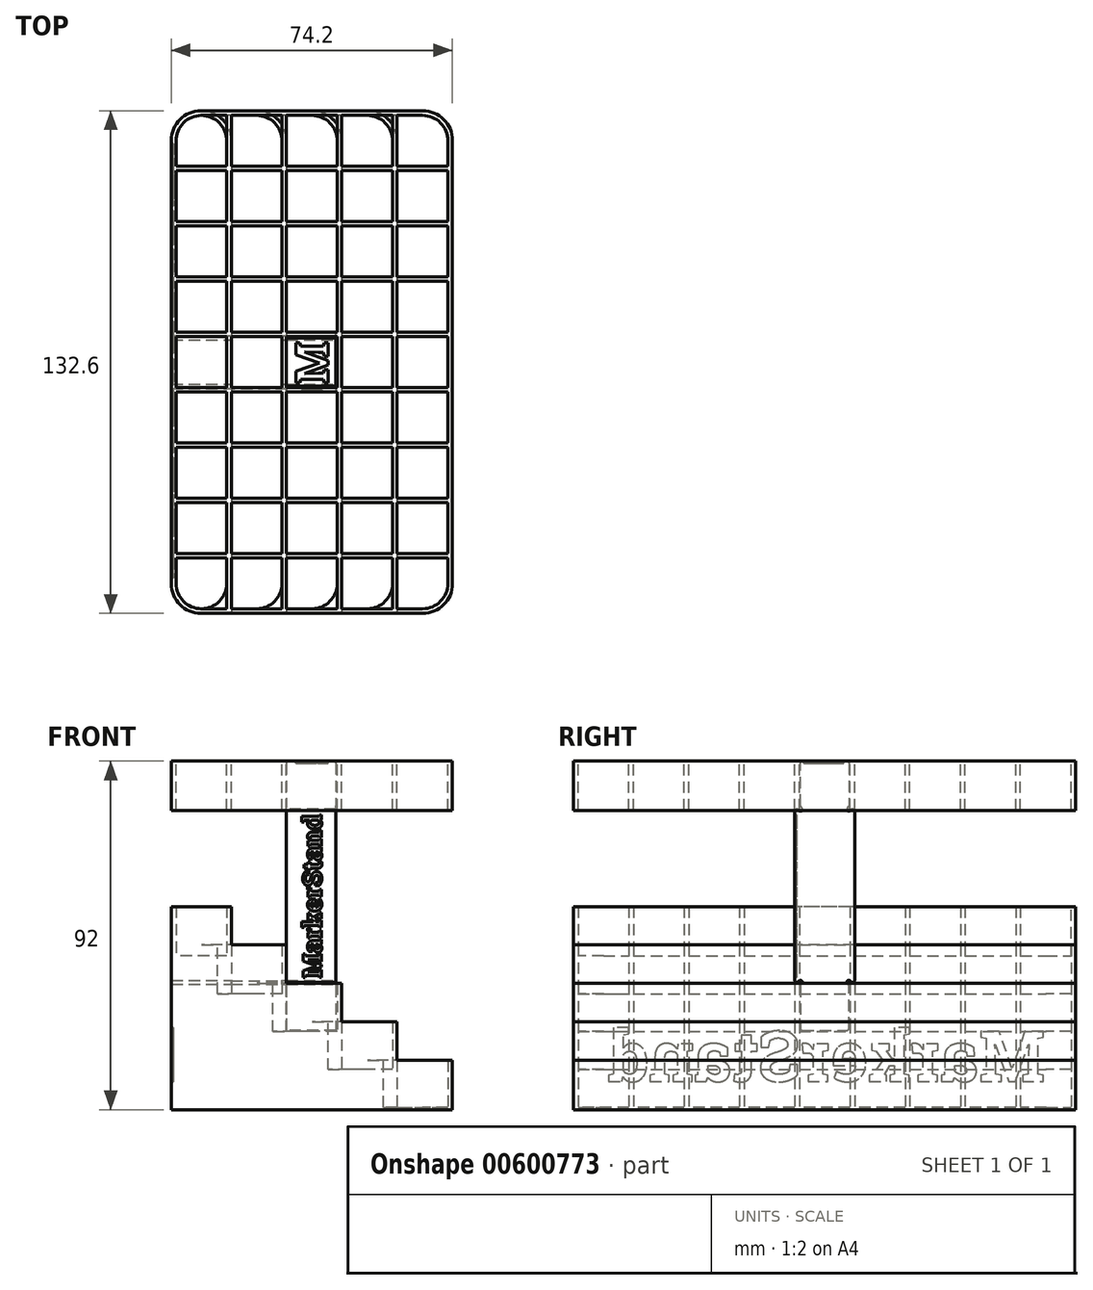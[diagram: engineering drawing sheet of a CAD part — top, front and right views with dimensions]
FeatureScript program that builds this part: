
annotation { "Feature Type Name" : "Feature", "Feature Type Description" : "" }
export const myFeature = defineFeature(function(context is Context, id is Id, definition is map)
    precondition{}
    {
        {
            var Q0;
            Q0=qCreatedBy(makeId("Top.planeOp"),FACE);
            var sketch = newSketch(context, id + "F0", { "sketchPlane" : qUnion([Q0])});
            skLineSegment(sketch, "E0.bottom", {"start": v(-37.1, 66.3) * mm, "end": v(37.1, 66.3) * mm});
            skLineSegment(sketch, "E0.top", {"start": v(-37.1, -66.3) * mm, "end": v(37.1, -66.3) * mm});
            skLineSegment(sketch, "E0.left", {"start": v(-37.1, 66.3) * mm, "end": v(-37.1, -66.3) * mm});
            skLineSegment(sketch, "E0.right", {"start": v(37.1, 66.3) * mm, "end": v(37.1, -66.3) * mm});
            skPoint(sketch, "E0.middle", {"position": v(0, 0) * mm});
            skLineSegment(sketch, "E1.bottom", {"start": v(-35.9, 65.1) * mm, "end": v(-22.5, 65.1) * mm});
            skLineSegment(sketch, "E1.top", {"start": v(-35.9, 51.7) * mm, "end": v(-22.5, 51.7) * mm});
            skLineSegment(sketch, "E1.left", {"start": v(-35.9, 65.1) * mm, "end": v(-35.9, 51.7) * mm});
            skLineSegment(sketch, "E1.right", {"start": v(-22.5, 65.1) * mm, "end": v(-22.5, 51.7) * mm});
            skLineSegment(sketch, "E2.0.1.0", {"start": v(-35.9, 37.1) * mm, "end": v(-22.5, 37.1) * mm});
            skLineSegment(sketch, "E2.0.1.1", {"start": v(-22.5, 50.5) * mm, "end": v(-22.5, 37.1) * mm});
            skLineSegment(sketch, "E2.0.1.2", {"start": v(-35.9, 50.5) * mm, "end": v(-22.5, 50.5) * mm});
            skLineSegment(sketch, "E2.0.1.3", {"start": v(-35.9, 50.5) * mm, "end": v(-35.9, 37.1) * mm});
            skLineSegment(sketch, "E2.0.2.0", {"start": v(-35.9, 22.5) * mm, "end": v(-22.5, 22.5) * mm});
            skLineSegment(sketch, "E2.0.2.1", {"start": v(-22.5, 35.9) * mm, "end": v(-22.5, 22.5) * mm});
            skLineSegment(sketch, "E2.0.2.2", {"start": v(-35.9, 35.9) * mm, "end": v(-22.5, 35.9) * mm});
            skLineSegment(sketch, "E2.0.2.3", {"start": v(-35.9, 35.9) * mm, "end": v(-35.9, 22.5) * mm});
            skLineSegment(sketch, "E2.0.3.0", {"start": v(-35.9, 7.9) * mm, "end": v(-22.5, 7.9) * mm});
            skLineSegment(sketch, "E2.0.3.1", {"start": v(-22.5, 21.3) * mm, "end": v(-22.5, 7.9) * mm});
            skLineSegment(sketch, "E2.0.3.2", {"start": v(-35.9, 21.3) * mm, "end": v(-22.5, 21.3) * mm});
            skLineSegment(sketch, "E2.0.3.3", {"start": v(-35.9, 21.3) * mm, "end": v(-35.9, 7.9) * mm});
            skLineSegment(sketch, "E2.0.4.0", {"start": v(-35.9, -6.7) * mm, "end": v(-22.5, -6.7) * mm});
            skLineSegment(sketch, "E2.0.4.1", {"start": v(-22.5, 6.7) * mm, "end": v(-22.5, -6.7) * mm});
            skLineSegment(sketch, "E2.0.4.2", {"start": v(-35.9, 6.7) * mm, "end": v(-22.5, 6.7) * mm});
            skLineSegment(sketch, "E2.0.4.3", {"start": v(-35.9, 6.7) * mm, "end": v(-35.9, -6.7) * mm});
            skLineSegment(sketch, "E2.0.5.0", {"start": v(-35.9, -21.3) * mm, "end": v(-22.5, -21.3) * mm});
            skLineSegment(sketch, "E2.0.5.1", {"start": v(-22.5, -7.9) * mm, "end": v(-22.5, -21.3) * mm});
            skLineSegment(sketch, "E2.0.5.2", {"start": v(-35.9, -7.9) * mm, "end": v(-22.5, -7.9) * mm});
            skLineSegment(sketch, "E2.0.5.3", {"start": v(-35.9, -7.9) * mm, "end": v(-35.9, -21.3) * mm});
            skLineSegment(sketch, "E2.0.6.0", {"start": v(-35.9, -35.9) * mm, "end": v(-22.5, -35.9) * mm});
            skLineSegment(sketch, "E2.0.6.1", {"start": v(-22.5, -22.5) * mm, "end": v(-22.5, -35.9) * mm});
            skLineSegment(sketch, "E2.0.6.2", {"start": v(-35.9, -22.5) * mm, "end": v(-22.5, -22.5) * mm});
            skLineSegment(sketch, "E2.0.6.3", {"start": v(-35.9, -22.5) * mm, "end": v(-35.9, -35.9) * mm});
            skLineSegment(sketch, "E2.0.7.0", {"start": v(-35.9, -50.5) * mm, "end": v(-22.5, -50.5) * mm});
            skLineSegment(sketch, "E2.0.7.1", {"start": v(-22.5, -37.1) * mm, "end": v(-22.5, -50.5) * mm});
            skLineSegment(sketch, "E2.0.7.2", {"start": v(-35.9, -37.1) * mm, "end": v(-22.5, -37.1) * mm});
            skLineSegment(sketch, "E2.0.7.3", {"start": v(-35.9, -37.1) * mm, "end": v(-35.9, -50.5) * mm});
            skLineSegment(sketch, "E2.0.8.0", {"start": v(-35.9, -65.1) * mm, "end": v(-22.5, -65.1) * mm});
            skLineSegment(sketch, "E2.0.8.1", {"start": v(-22.5, -51.7) * mm, "end": v(-22.5, -65.1) * mm});
            skLineSegment(sketch, "E2.0.8.2", {"start": v(-35.9, -51.7) * mm, "end": v(-22.5, -51.7) * mm});
            skLineSegment(sketch, "E2.0.8.3", {"start": v(-35.9, -51.7) * mm, "end": v(-35.9, -65.1) * mm});
            skLineSegment(sketch, "E2.1.0.0", {"start": v(-21.3, 51.7) * mm, "end": v(-7.9, 51.7) * mm});
            skLineSegment(sketch, "E2.1.0.1", {"start": v(-7.9, 65.1) * mm, "end": v(-7.9, 51.7) * mm});
            skLineSegment(sketch, "E2.1.0.2", {"start": v(-21.3, 65.1) * mm, "end": v(-7.9, 65.1) * mm});
            skLineSegment(sketch, "E2.1.0.3", {"start": v(-21.3, 65.1) * mm, "end": v(-21.3, 51.7) * mm});
            skLineSegment(sketch, "E2.1.1.0", {"start": v(-21.3, 37.1) * mm, "end": v(-7.9, 37.1) * mm});
            skLineSegment(sketch, "E2.1.1.1", {"start": v(-7.9, 50.5) * mm, "end": v(-7.9, 37.1) * mm});
            skLineSegment(sketch, "E2.1.1.2", {"start": v(-21.3, 50.5) * mm, "end": v(-7.9, 50.5) * mm});
            skLineSegment(sketch, "E2.1.1.3", {"start": v(-21.3, 50.5) * mm, "end": v(-21.3, 37.1) * mm});
            skLineSegment(sketch, "E2.1.2.0", {"start": v(-21.3, 22.5) * mm, "end": v(-7.9, 22.5) * mm});
            skLineSegment(sketch, "E2.1.2.1", {"start": v(-7.9, 35.9) * mm, "end": v(-7.9, 22.5) * mm});
            skLineSegment(sketch, "E2.1.2.2", {"start": v(-21.3, 35.9) * mm, "end": v(-7.9, 35.9) * mm});
            skLineSegment(sketch, "E2.1.2.3", {"start": v(-21.3, 35.9) * mm, "end": v(-21.3, 22.5) * mm});
            skLineSegment(sketch, "E2.1.3.0", {"start": v(-21.3, 7.9) * mm, "end": v(-7.9, 7.9) * mm});
            skLineSegment(sketch, "E2.1.3.1", {"start": v(-7.9, 21.3) * mm, "end": v(-7.9, 7.9) * mm});
            skLineSegment(sketch, "E2.1.3.2", {"start": v(-21.3, 21.3) * mm, "end": v(-7.9, 21.3) * mm});
            skLineSegment(sketch, "E2.1.3.3", {"start": v(-21.3, 21.3) * mm, "end": v(-21.3, 7.9) * mm});
            skLineSegment(sketch, "E2.1.4.0", {"start": v(-21.3, -6.7) * mm, "end": v(-7.9, -6.7) * mm});
            skLineSegment(sketch, "E2.1.4.1", {"start": v(-7.9, 6.7) * mm, "end": v(-7.9, -6.7) * mm});
            skLineSegment(sketch, "E2.1.4.2", {"start": v(-21.3, 6.7) * mm, "end": v(-7.9, 6.7) * mm});
            skLineSegment(sketch, "E2.1.4.3", {"start": v(-21.3, 6.7) * mm, "end": v(-21.3, -6.7) * mm});
            skLineSegment(sketch, "E2.1.5.0", {"start": v(-21.3, -21.3) * mm, "end": v(-7.9, -21.3) * mm});
            skLineSegment(sketch, "E2.1.5.1", {"start": v(-7.9, -7.9) * mm, "end": v(-7.9, -21.3) * mm});
            skLineSegment(sketch, "E2.1.5.2", {"start": v(-21.3, -7.9) * mm, "end": v(-7.9, -7.9) * mm});
            skLineSegment(sketch, "E2.1.5.3", {"start": v(-21.3, -7.9) * mm, "end": v(-21.3, -21.3) * mm});
            skLineSegment(sketch, "E2.1.6.0", {"start": v(-21.3, -35.9) * mm, "end": v(-7.9, -35.9) * mm});
            skLineSegment(sketch, "E2.1.6.1", {"start": v(-7.9, -22.5) * mm, "end": v(-7.9, -35.9) * mm});
            skLineSegment(sketch, "E2.1.6.2", {"start": v(-21.3, -22.5) * mm, "end": v(-7.9, -22.5) * mm});
            skLineSegment(sketch, "E2.1.6.3", {"start": v(-21.3, -22.5) * mm, "end": v(-21.3, -35.9) * mm});
            skLineSegment(sketch, "E2.1.7.0", {"start": v(-21.3, -50.5) * mm, "end": v(-7.9, -50.5) * mm});
            skLineSegment(sketch, "E2.1.7.1", {"start": v(-7.9, -37.1) * mm, "end": v(-7.9, -50.5) * mm});
            skLineSegment(sketch, "E2.1.7.2", {"start": v(-21.3, -37.1) * mm, "end": v(-7.9, -37.1) * mm});
            skLineSegment(sketch, "E2.1.7.3", {"start": v(-21.3, -37.1) * mm, "end": v(-21.3, -50.5) * mm});
            skLineSegment(sketch, "E2.1.8.0", {"start": v(-21.3, -65.1) * mm, "end": v(-7.9, -65.1) * mm});
            skLineSegment(sketch, "E2.1.8.1", {"start": v(-7.9, -51.7) * mm, "end": v(-7.9, -65.1) * mm});
            skLineSegment(sketch, "E2.1.8.2", {"start": v(-21.3, -51.7) * mm, "end": v(-7.9, -51.7) * mm});
            skLineSegment(sketch, "E2.1.8.3", {"start": v(-21.3, -51.7) * mm, "end": v(-21.3, -65.1) * mm});
            skLineSegment(sketch, "E2.2.0.0", {"start": v(-6.7, 51.7) * mm, "end": v(6.7, 51.7) * mm});
            skLineSegment(sketch, "E2.2.0.1", {"start": v(6.7, 65.1) * mm, "end": v(6.7, 51.7) * mm});
            skLineSegment(sketch, "E2.2.0.2", {"start": v(-6.7, 65.1) * mm, "end": v(6.7, 65.1) * mm});
            skLineSegment(sketch, "E2.2.0.3", {"start": v(-6.7, 65.1) * mm, "end": v(-6.7, 51.7) * mm});
            skLineSegment(sketch, "E2.2.1.0", {"start": v(-6.7, 37.1) * mm, "end": v(6.7, 37.1) * mm});
            skLineSegment(sketch, "E2.2.1.1", {"start": v(6.7, 50.5) * mm, "end": v(6.7, 37.1) * mm});
            skLineSegment(sketch, "E2.2.1.2", {"start": v(-6.7, 50.5) * mm, "end": v(6.7, 50.5) * mm});
            skLineSegment(sketch, "E2.2.1.3", {"start": v(-6.7, 50.5) * mm, "end": v(-6.7, 37.1) * mm});
            skLineSegment(sketch, "E2.2.2.0", {"start": v(-6.7, 22.5) * mm, "end": v(6.7, 22.5) * mm});
            skLineSegment(sketch, "E2.2.2.1", {"start": v(6.7, 35.9) * mm, "end": v(6.7, 22.5) * mm});
            skLineSegment(sketch, "E2.2.2.2", {"start": v(-6.7, 35.9) * mm, "end": v(6.7, 35.9) * mm});
            skLineSegment(sketch, "E2.2.2.3", {"start": v(-6.7, 35.9) * mm, "end": v(-6.7, 22.5) * mm});
            skLineSegment(sketch, "E2.2.3.0", {"start": v(-6.7, 7.9) * mm, "end": v(6.7, 7.9) * mm});
            skLineSegment(sketch, "E2.2.3.1", {"start": v(6.7, 21.3) * mm, "end": v(6.7, 7.9) * mm});
            skLineSegment(sketch, "E2.2.3.2", {"start": v(-6.7, 21.3) * mm, "end": v(6.7, 21.3) * mm});
            skLineSegment(sketch, "E2.2.3.3", {"start": v(-6.7, 21.3) * mm, "end": v(-6.7, 7.9) * mm});
            skLineSegment(sketch, "E2.2.4.0", {"start": v(-6.7, -6.7) * mm, "end": v(6.7, -6.7) * mm});
            skLineSegment(sketch, "E2.2.4.1", {"start": v(6.7, 6.7) * mm, "end": v(6.7, -6.7) * mm});
            skLineSegment(sketch, "E2.2.4.2", {"start": v(-6.7, 6.7) * mm, "end": v(6.7, 6.7) * mm});
            skLineSegment(sketch, "E2.2.4.3", {"start": v(-6.7, 6.7) * mm, "end": v(-6.7, -6.7) * mm});
            skLineSegment(sketch, "E2.2.5.0", {"start": v(-6.7, -21.3) * mm, "end": v(6.7, -21.3) * mm});
            skLineSegment(sketch, "E2.2.5.1", {"start": v(6.7, -7.9) * mm, "end": v(6.7, -21.3) * mm});
            skLineSegment(sketch, "E2.2.5.2", {"start": v(-6.7, -7.9) * mm, "end": v(6.7, -7.9) * mm});
            skLineSegment(sketch, "E2.2.5.3", {"start": v(-6.7, -7.9) * mm, "end": v(-6.7, -21.3) * mm});
            skLineSegment(sketch, "E2.2.6.0", {"start": v(-6.7, -35.9) * mm, "end": v(6.7, -35.9) * mm});
            skLineSegment(sketch, "E2.2.6.1", {"start": v(6.7, -22.5) * mm, "end": v(6.7, -35.9) * mm});
            skLineSegment(sketch, "E2.2.6.2", {"start": v(-6.7, -22.5) * mm, "end": v(6.7, -22.5) * mm});
            skLineSegment(sketch, "E2.2.6.3", {"start": v(-6.7, -22.5) * mm, "end": v(-6.7, -35.9) * mm});
            skLineSegment(sketch, "E2.2.7.0", {"start": v(-6.7, -50.5) * mm, "end": v(6.7, -50.5) * mm});
            skLineSegment(sketch, "E2.2.7.1", {"start": v(6.7, -37.1) * mm, "end": v(6.7, -50.5) * mm});
            skLineSegment(sketch, "E2.2.7.2", {"start": v(-6.7, -37.1) * mm, "end": v(6.7, -37.1) * mm});
            skLineSegment(sketch, "E2.2.7.3", {"start": v(-6.7, -37.1) * mm, "end": v(-6.7, -50.5) * mm});
            skLineSegment(sketch, "E2.2.8.0", {"start": v(-6.7, -65.1) * mm, "end": v(6.7, -65.1) * mm});
            skLineSegment(sketch, "E2.2.8.1", {"start": v(6.7, -51.7) * mm, "end": v(6.7, -65.1) * mm});
            skLineSegment(sketch, "E2.2.8.2", {"start": v(-6.7, -51.7) * mm, "end": v(6.7, -51.7) * mm});
            skLineSegment(sketch, "E2.2.8.3", {"start": v(-6.7, -51.7) * mm, "end": v(-6.7, -65.1) * mm});
            skLineSegment(sketch, "E2.3.0.0", {"start": v(7.9, 51.7) * mm, "end": v(21.3, 51.7) * mm});
            skLineSegment(sketch, "E2.3.0.1", {"start": v(21.3, 65.1) * mm, "end": v(21.3, 51.7) * mm});
            skLineSegment(sketch, "E2.3.0.2", {"start": v(7.9, 65.1) * mm, "end": v(21.3, 65.1) * mm});
            skLineSegment(sketch, "E2.3.0.3", {"start": v(7.9, 65.1) * mm, "end": v(7.9, 51.7) * mm});
            skLineSegment(sketch, "E2.3.1.0", {"start": v(7.9, 37.1) * mm, "end": v(21.3, 37.1) * mm});
            skLineSegment(sketch, "E2.3.1.1", {"start": v(21.3, 50.5) * mm, "end": v(21.3, 37.1) * mm});
            skLineSegment(sketch, "E2.3.1.2", {"start": v(7.9, 50.5) * mm, "end": v(21.3, 50.5) * mm});
            skLineSegment(sketch, "E2.3.1.3", {"start": v(7.9, 50.5) * mm, "end": v(7.9, 37.1) * mm});
            skLineSegment(sketch, "E2.3.2.0", {"start": v(7.9, 22.5) * mm, "end": v(21.3, 22.5) * mm});
            skLineSegment(sketch, "E2.3.2.1", {"start": v(21.3, 35.9) * mm, "end": v(21.3, 22.5) * mm});
            skLineSegment(sketch, "E2.3.2.2", {"start": v(7.9, 35.9) * mm, "end": v(21.3, 35.9) * mm});
            skLineSegment(sketch, "E2.3.2.3", {"start": v(7.9, 35.9) * mm, "end": v(7.9, 22.5) * mm});
            skLineSegment(sketch, "E2.3.3.0", {"start": v(7.9, 7.9) * mm, "end": v(21.3, 7.9) * mm});
            skLineSegment(sketch, "E2.3.3.1", {"start": v(21.3, 21.3) * mm, "end": v(21.3, 7.9) * mm});
            skLineSegment(sketch, "E2.3.3.2", {"start": v(7.9, 21.3) * mm, "end": v(21.3, 21.3) * mm});
            skLineSegment(sketch, "E2.3.3.3", {"start": v(7.9, 21.3) * mm, "end": v(7.9, 7.9) * mm});
            skLineSegment(sketch, "E2.3.4.0", {"start": v(7.9, -6.7) * mm, "end": v(21.3, -6.7) * mm});
            skLineSegment(sketch, "E2.3.4.1", {"start": v(21.3, 6.7) * mm, "end": v(21.3, -6.7) * mm});
            skLineSegment(sketch, "E2.3.4.2", {"start": v(7.9, 6.7) * mm, "end": v(21.3, 6.7) * mm});
            skLineSegment(sketch, "E2.3.4.3", {"start": v(7.9, 6.7) * mm, "end": v(7.9, -6.7) * mm});
            skLineSegment(sketch, "E2.3.5.0", {"start": v(7.9, -21.3) * mm, "end": v(21.3, -21.3) * mm});
            skLineSegment(sketch, "E2.3.5.1", {"start": v(21.3, -7.9) * mm, "end": v(21.3, -21.3) * mm});
            skLineSegment(sketch, "E2.3.5.2", {"start": v(7.9, -7.9) * mm, "end": v(21.3, -7.9) * mm});
            skLineSegment(sketch, "E2.3.5.3", {"start": v(7.9, -7.9) * mm, "end": v(7.9, -21.3) * mm});
            skLineSegment(sketch, "E2.3.6.0", {"start": v(7.9, -35.9) * mm, "end": v(21.3, -35.9) * mm});
            skLineSegment(sketch, "E2.3.6.1", {"start": v(21.3, -22.5) * mm, "end": v(21.3, -35.9) * mm});
            skLineSegment(sketch, "E2.3.6.2", {"start": v(7.9, -22.5) * mm, "end": v(21.3, -22.5) * mm});
            skLineSegment(sketch, "E2.3.6.3", {"start": v(7.9, -22.5) * mm, "end": v(7.9, -35.9) * mm});
            skLineSegment(sketch, "E2.3.7.0", {"start": v(7.9, -50.5) * mm, "end": v(21.3, -50.5) * mm});
            skLineSegment(sketch, "E2.3.7.1", {"start": v(21.3, -37.1) * mm, "end": v(21.3, -50.5) * mm});
            skLineSegment(sketch, "E2.3.7.2", {"start": v(7.9, -37.1) * mm, "end": v(21.3, -37.1) * mm});
            skLineSegment(sketch, "E2.3.7.3", {"start": v(7.9, -37.1) * mm, "end": v(7.9, -50.5) * mm});
            skLineSegment(sketch, "E2.3.8.0", {"start": v(7.9, -65.1) * mm, "end": v(21.3, -65.1) * mm});
            skLineSegment(sketch, "E2.3.8.1", {"start": v(21.3, -51.7) * mm, "end": v(21.3, -65.1) * mm});
            skLineSegment(sketch, "E2.3.8.2", {"start": v(7.9, -51.7) * mm, "end": v(21.3, -51.7) * mm});
            skLineSegment(sketch, "E2.3.8.3", {"start": v(7.9, -51.7) * mm, "end": v(7.9, -65.1) * mm});
            skLineSegment(sketch, "E2.4.0.0", {"start": v(22.5, 51.7) * mm, "end": v(35.9, 51.7) * mm});
            skLineSegment(sketch, "E2.4.0.1", {"start": v(35.9, 65.1) * mm, "end": v(35.9, 51.7) * mm});
            skLineSegment(sketch, "E2.4.0.2", {"start": v(22.5, 65.1) * mm, "end": v(35.9, 65.1) * mm});
            skLineSegment(sketch, "E2.4.0.3", {"start": v(22.5, 65.1) * mm, "end": v(22.5, 51.7) * mm});
            skLineSegment(sketch, "E2.4.1.0", {"start": v(22.5, 37.1) * mm, "end": v(35.9, 37.1) * mm});
            skLineSegment(sketch, "E2.4.1.1", {"start": v(35.9, 50.5) * mm, "end": v(35.9, 37.1) * mm});
            skLineSegment(sketch, "E2.4.1.2", {"start": v(22.5, 50.5) * mm, "end": v(35.9, 50.5) * mm});
            skLineSegment(sketch, "E2.4.1.3", {"start": v(22.5, 50.5) * mm, "end": v(22.5, 37.1) * mm});
            skLineSegment(sketch, "E2.4.2.0", {"start": v(22.5, 22.5) * mm, "end": v(35.9, 22.5) * mm});
            skLineSegment(sketch, "E2.4.2.1", {"start": v(35.9, 35.9) * mm, "end": v(35.9, 22.5) * mm});
            skLineSegment(sketch, "E2.4.2.2", {"start": v(22.5, 35.9) * mm, "end": v(35.9, 35.9) * mm});
            skLineSegment(sketch, "E2.4.2.3", {"start": v(22.5, 35.9) * mm, "end": v(22.5, 22.5) * mm});
            skLineSegment(sketch, "E2.4.3.0", {"start": v(22.5, 7.9) * mm, "end": v(35.9, 7.9) * mm});
            skLineSegment(sketch, "E2.4.3.1", {"start": v(35.9, 21.3) * mm, "end": v(35.9, 7.9) * mm});
            skLineSegment(sketch, "E2.4.3.2", {"start": v(22.5, 21.3) * mm, "end": v(35.9, 21.3) * mm});
            skLineSegment(sketch, "E2.4.3.3", {"start": v(22.5, 21.3) * mm, "end": v(22.5, 7.9) * mm});
            skLineSegment(sketch, "E2.4.4.0", {"start": v(22.5, -6.7) * mm, "end": v(35.9, -6.7) * mm});
            skLineSegment(sketch, "E2.4.4.1", {"start": v(35.9, 6.7) * mm, "end": v(35.9, -6.7) * mm});
            skLineSegment(sketch, "E2.4.4.2", {"start": v(22.5, 6.7) * mm, "end": v(35.9, 6.7) * mm});
            skLineSegment(sketch, "E2.4.4.3", {"start": v(22.5, 6.7) * mm, "end": v(22.5, -6.7) * mm});
            skLineSegment(sketch, "E2.4.5.0", {"start": v(22.5, -21.3) * mm, "end": v(35.9, -21.3) * mm});
            skLineSegment(sketch, "E2.4.5.1", {"start": v(35.9, -7.9) * mm, "end": v(35.9, -21.3) * mm});
            skLineSegment(sketch, "E2.4.5.2", {"start": v(22.5, -7.9) * mm, "end": v(35.9, -7.9) * mm});
            skLineSegment(sketch, "E2.4.5.3", {"start": v(22.5, -7.9) * mm, "end": v(22.5, -21.3) * mm});
            skLineSegment(sketch, "E2.4.6.0", {"start": v(22.5, -35.9) * mm, "end": v(35.9, -35.9) * mm});
            skLineSegment(sketch, "E2.4.6.1", {"start": v(35.9, -22.5) * mm, "end": v(35.9, -35.9) * mm});
            skLineSegment(sketch, "E2.4.6.2", {"start": v(22.5, -22.5) * mm, "end": v(35.9, -22.5) * mm});
            skLineSegment(sketch, "E2.4.6.3", {"start": v(22.5, -22.5) * mm, "end": v(22.5, -35.9) * mm});
            skLineSegment(sketch, "E2.4.7.0", {"start": v(22.5, -50.5) * mm, "end": v(35.9, -50.5) * mm});
            skLineSegment(sketch, "E2.4.7.1", {"start": v(35.9, -37.1) * mm, "end": v(35.9, -50.5) * mm});
            skLineSegment(sketch, "E2.4.7.2", {"start": v(22.5, -37.1) * mm, "end": v(35.9, -37.1) * mm});
            skLineSegment(sketch, "E2.4.7.3", {"start": v(22.5, -37.1) * mm, "end": v(22.5, -50.5) * mm});
            skLineSegment(sketch, "E2.4.8.0", {"start": v(22.5, -65.1) * mm, "end": v(35.9, -65.1) * mm});
            skLineSegment(sketch, "E2.4.8.1", {"start": v(35.9, -51.7) * mm, "end": v(35.9, -65.1) * mm});
            skLineSegment(sketch, "E2.4.8.2", {"start": v(22.5, -51.7) * mm, "end": v(35.9, -51.7) * mm});
            skLineSegment(sketch, "E2.4.8.3", {"start": v(22.5, -51.7) * mm, "end": v(22.5, -65.1) * mm});
            skLineSegment(sketch, "E2.direction1", {"start": v(-35.9, 51.7) * mm, "end": v(-21.3, 51.7) * mm, "construction": true});
            skLineSegment(sketch, "E2.direction2", {"start": v(-35.9, 51.7) * mm, "end": v(-35.9, 37.1) * mm, "construction": true});
            skSolve(sketch);
        }
        {
            var Q0;
            Q0 = qSketchRegion(id + "F0", true);
            extrude(context, id + "F1", {"entities" : qUnion([Q0]), "depth" : 53 * mm, "offsetDistance" : 25 * mm});
        }
        {
            var Q0;
            Q0=makeQuery(id+"F1.opExtrude","SWEPT_FACE",FACE,{"disambiguationData":[OSD([sQuery(id+"F0.wireOp",EDGE,"E0.bottom")])]});
            var sketch = newSketch(context, id + "F2", { "sketchPlane" : qUnion([Q0])});
            skLineSegment(sketch, "E3", {"start": v(37.1, -0.6) * mm, "end": v(-37.1, -0.6) * mm});
            skLineSegment(sketch, "E4", {"start": v(-37.1, -0.6) * mm, "end": v(-37.1, 0) * mm});
            skLineSegment(sketch, "E5", {"start": v(-37.1, 0) * mm, "end": v(-22.5, 0) * mm});
            skLineSegment(sketch, "E6", {"start": v(-22.5, 0) * mm, "end": v(-22.5, 10) * mm});
            skLineSegment(sketch, "E7", {"start": v(-22.5, 10) * mm, "end": v(-7.9, 10) * mm});
            skLineSegment(sketch, "E8", {"start": v(-7.9, 10) * mm, "end": v(-7.9, 20) * mm});
            skLineSegment(sketch, "E9", {"start": v(-7.9, 20) * mm, "end": v(6.7, 20) * mm});
            skLineSegment(sketch, "E10", {"start": v(6.7, 20) * mm, "end": v(6.7, 30) * mm});
            skLineSegment(sketch, "E11", {"start": v(6.7, 30) * mm, "end": v(21.3, 30) * mm});
            skLineSegment(sketch, "E12", {"start": v(21.3, 30) * mm, "end": v(21.3, 40) * mm});
            skLineSegment(sketch, "E13", {"start": v(21.3, 40) * mm, "end": v(37.1, 40) * mm});
            skLineSegment(sketch, "E14", {"start": v(37.1, 40) * mm, "end": v(37.1, -0.6) * mm});
            skSolve(sketch);
        }
        {
            var Q0;
            Q0 = qSketchRegion(id + "F2", true);
            var Q1;
            Q1=makeQuery(id+"F1.opExtrude","SWEPT_FACE",FACE,{"disambiguationData":[OSD([sQuery(id+"F0.wireOp",EDGE,"E0.top")])]});
            extrude(context, id + "F3", {"entities" : qUnion([Q0]), "operationType" : NewBodyOperationType.ADD, "endBound" : BoundingType.UP_TO_SURFACE, "oppositeDirection" : true, "depth" : 25 * mm, "endBoundEntityFace" : qUnion([Q1]), "offsetDistance" : 25 * mm});
        }
        {
            var Q0;
            {var subQ0=sQuery(id+"F0.wireOp",EDGE,"E0.top");Q0=makeQuery(id+"F3.boolean.opBoolean","MERGE",FACE,{"derivedFrom":[makeQuery(id+"F1.opExtrude","SWEPT_FACE",FACE,{"disambiguationData":[OSD([subQ0])]}),makeQuery(id+"F3.opExtrude","CAP_FACE",FACE,{"disambiguationData":[OSD([subQ0])],"isStart":false})]});}
            var sketch = newSketch(context, id + "F4", { "sketchPlane" : qUnion([Q0])});
            skLineSegment(sketch, "E15", {"start": v(-21.3, 53) * mm, "end": v(-21.3, 42.85) * mm});
            skLineSegment(sketch, "E16", {"start": v(-21.3, 42.85) * mm, "end": v(-6.7, 42.85) * mm});
            skLineSegment(sketch, "E17", {"start": v(-6.7, 42.85) * mm, "end": v(-6.7, 32.7) * mm});
            skLineSegment(sketch, "E18", {"start": v(-6.7, 32.7) * mm, "end": v(7.9, 32.7) * mm});
            skLineSegment(sketch, "E19", {"start": v(7.9, 32.7) * mm, "end": v(7.9, 22.55) * mm});
            skLineSegment(sketch, "E20", {"start": v(7.9, 22.55) * mm, "end": v(22.5, 22.55) * mm});
            skLineSegment(sketch, "E21", {"start": v(22.5, 22.55) * mm, "end": v(22.5, 12.4) * mm});
            skLineSegment(sketch, "E22", {"start": v(22.5, 12.4) * mm, "end": v(37.1, 12.4) * mm});
            skLineSegment(sketch, "E23", {"start": v(37.1, 12.4) * mm, "end": v(37.1, 53) * mm});
            skLineSegment(sketch, "E24", {"start": v(37.1, 53) * mm, "end": v(-21.3, 53) * mm});
            skLineSegment(sketch, "E25", {"start": v(-21.3, 42.85) * mm, "end": v(7.9, 22.55) * mm, "construction": true});
            skSolve(sketch);
        }
        {
            var Q0;
            Q0 = qSketchRegion(id + "F4", true);
            extrude(context, id + "F5", {"entities" : qUnion([Q0]), "operationType" : NewBodyOperationType.REMOVE, "endBound" : BoundingType.THROUGH_ALL, "oppositeDirection" : true, "depth" : 25 * mm, "offsetDistance" : 25 * mm});
        }
        {
            var Q0;
            Q0=makeQuery(id+"F3.boolean.opBoolean","MERGE",FACE,{"derivedFrom":[makeQuery(id+"F1.opExtrude","SWEPT_FACE",FACE,{"disambiguationData":[OSD([sQuery(id+"F0.wireOp",EDGE,"E0.left")])]}),makeQuery(id+"F3.opExtrude","SWEPT_FACE",FACE,{"disambiguationData":[OSD([sQuery(id+"F2.wireOp",EDGE,"E14")])]})]});
            var sketch = newSketch(context, id + "F6", { "sketchPlane" : qUnion([Q0])});
            skLineSegment(sketch, "E26", {"start": v(0, 0) * mm, "end": v(0, 40) * mm, "construction": true});
            skText(sketch, "E27", { "text": "MarkerStand", "fontName": "RobotoSlab-Bold.ttf"});
            const initialGuessF6  = {"E27": [-0.0582, 0.0069, 1, 0, 0.01335]};
            skSetInitialGuess(sketch, initialGuessF6);
            skSolve(sketch);
        }
        {
            var Q0;
            Q0 = qSketchRegion(id + "F6", true);
            extrude(context, id + "F7", {"entities" : qUnion([Q0]), "operationType" : NewBodyOperationType.REMOVE, "oppositeDirection" : true, "depth" : 0.54 * mm, "offsetDistance" : 25 * mm});
        }
        {
            var Q0;
            Q0=makeQuery(id+"F1.opExtrude","SWEPT_EDGE",EDGE,{"disambiguationData":[OSD([sQuery(id+"F0.wireOp",EDGE,"E1.bottom"),sQuery(id+"F0.wireOp",EDGE,"E1.right")])]});
            var Q1;
            Q1=makeQuery(id+"F1.opExtrude","SWEPT_EDGE",EDGE,{"disambiguationData":[OSD([sQuery(id+"F0.wireOp",EDGE,"E2.1.0.1"),sQuery(id+"F0.wireOp",EDGE,"E2.1.0.2")])]});
            var Q2;
            Q2=makeQuery(id+"F1.opExtrude","SWEPT_EDGE",EDGE,{"disambiguationData":[OSD([sQuery(id+"F0.wireOp",EDGE,"E2.2.0.1"),sQuery(id+"F0.wireOp",EDGE,"E2.2.0.2")])]});
            var Q3;
            Q3=makeQuery(id+"F1.opExtrude","SWEPT_EDGE",EDGE,{"disambiguationData":[OSD([sQuery(id+"F0.wireOp",EDGE,"E2.3.0.1"),sQuery(id+"F0.wireOp",EDGE,"E2.3.0.2")])]});
            var Q4;
            Q4=makeQuery(id+"F1.opExtrude","SWEPT_EDGE",EDGE,{"disambiguationData":[OSD([sQuery(id+"F0.wireOp",EDGE,"E2.4.0.1"),sQuery(id+"F0.wireOp",EDGE,"E2.4.0.2")])]});
            var Q5;
            Q5=makeQuery(id+"F1.opExtrude","SWEPT_EDGE",EDGE,{"disambiguationData":[OSD([sQuery(id+"F0.wireOp",EDGE,"E2.4.8.0"),sQuery(id+"F0.wireOp",EDGE,"E2.4.8.1")])]});
            var Q6;
            Q6=makeQuery(id+"F1.opExtrude","SWEPT_EDGE",EDGE,{"disambiguationData":[OSD([sQuery(id+"F0.wireOp",EDGE,"E2.3.8.0"),sQuery(id+"F0.wireOp",EDGE,"E2.3.8.1")])]});
            var Q7;
            Q7=makeQuery(id+"F1.opExtrude","SWEPT_EDGE",EDGE,{"disambiguationData":[OSD([sQuery(id+"F0.wireOp",EDGE,"E2.2.8.0"),sQuery(id+"F0.wireOp",EDGE,"E2.2.8.1")])]});
            var Q8;
            Q8=makeQuery(id+"F1.opExtrude","SWEPT_EDGE",EDGE,{"disambiguationData":[OSD([sQuery(id+"F0.wireOp",EDGE,"E2.1.8.0"),sQuery(id+"F0.wireOp",EDGE,"E2.1.8.1")])]});
            var Q9;
            Q9=makeQuery(id+"F1.opExtrude","SWEPT_EDGE",EDGE,{"disambiguationData":[OSD([sQuery(id+"F0.wireOp",EDGE,"E2.0.8.0"),sQuery(id+"F0.wireOp",EDGE,"E2.0.8.1")])]});
            var Q10;
            Q10=makeQuery(id+"F1.opExtrude","SWEPT_EDGE",EDGE,{"disambiguationData":[OSD([sQuery(id+"F0.wireOp",EDGE,"E2.0.8.0"),sQuery(id+"F0.wireOp",EDGE,"E2.0.8.3")])]});
            var Q11;
            Q11=makeQuery(id+"F1.opExtrude","SWEPT_EDGE",EDGE,{"disambiguationData":[OSD([sQuery(id+"F0.wireOp",EDGE,"E1.bottom"),sQuery(id+"F0.wireOp",EDGE,"E1.left")])]});
            fillet(context, id + "F8", {"entities" : qUnion([Q0, Q1, Q2, Q3, Q4, Q5, Q6, Q7, Q8, Q9, Q10, Q11]), "radius" : 6.7 * mm, "tangentPropagation" : true, "allowEdgeOverflow" : false});
        }
        {
            var Q0;
            Q0=makeQuery(id+"F5.boolean.opBoolean","INTERSECT",EDGE,{"derivedFrom":[makeQuery(id+"F3.boolean.opBoolean","MERGE",FACE,{"derivedFrom":[makeQuery(id+"F1.opExtrude","SWEPT_FACE",FACE,{"disambiguationData":[OSD([sQuery(id+"F0.wireOp",EDGE,"E0.bottom")])]}),makeQuery(id+"F3.opExtrude","CAP_FACE",FACE,{"disambiguationData":[OSD([sQuery(id+"F2.wireOp",EDGE,"E3"),sQuery(id+"F2.wireOp",EDGE,"E4"),sQuery(id+"F2.wireOp",EDGE,"E5"),sQuery(id+"F2.wireOp",EDGE,"E6"),sQuery(id+"F2.wireOp",EDGE,"E7"),sQuery(id+"F2.wireOp",EDGE,"E8"),sQuery(id+"F2.wireOp",EDGE,"E9"),sQuery(id+"F2.wireOp",EDGE,"E10"),sQuery(id+"F2.wireOp",EDGE,"E11"),sQuery(id+"F2.wireOp",EDGE,"E12"),sQuery(id+"F2.wireOp",EDGE,"E13"),sQuery(id+"F2.wireOp",EDGE,"E14")])],"isStart":true})]}),makeQuery(id+"F5.opExtrude","SWEPT_FACE",FACE,{"disambiguationData":[OSD([sQuery(id+"F4.wireOp",EDGE,"E15")])]})]});
            var Q1;
            Q1=makeQuery(id+"F5.boolean.opBoolean","INTERSECT",EDGE,{"derivedFrom":[makeQuery(id+"F3.boolean.opBoolean","MERGE",FACE,{"derivedFrom":[makeQuery(id+"F1.opExtrude","SWEPT_FACE",FACE,{"disambiguationData":[OSD([sQuery(id+"F0.wireOp",EDGE,"E0.bottom")])]}),makeQuery(id+"F3.opExtrude","CAP_FACE",FACE,{"disambiguationData":[OSD([sQuery(id+"F2.wireOp",EDGE,"E3"),sQuery(id+"F2.wireOp",EDGE,"E4"),sQuery(id+"F2.wireOp",EDGE,"E5"),sQuery(id+"F2.wireOp",EDGE,"E6"),sQuery(id+"F2.wireOp",EDGE,"E7"),sQuery(id+"F2.wireOp",EDGE,"E8"),sQuery(id+"F2.wireOp",EDGE,"E9"),sQuery(id+"F2.wireOp",EDGE,"E10"),sQuery(id+"F2.wireOp",EDGE,"E11"),sQuery(id+"F2.wireOp",EDGE,"E12"),sQuery(id+"F2.wireOp",EDGE,"E13"),sQuery(id+"F2.wireOp",EDGE,"E14")])],"isStart":true})]}),makeQuery(id+"F5.opExtrude","SWEPT_FACE",FACE,{"disambiguationData":[OSD([sQuery(id+"F4.wireOp",EDGE,"E17")])]})]});
            var Q2;
            Q2=makeQuery(id+"F5.boolean.opBoolean","INTERSECT",EDGE,{"derivedFrom":[makeQuery(id+"F3.boolean.opBoolean","MERGE",FACE,{"derivedFrom":[makeQuery(id+"F1.opExtrude","SWEPT_FACE",FACE,{"disambiguationData":[OSD([sQuery(id+"F0.wireOp",EDGE,"E0.bottom")])]}),makeQuery(id+"F3.opExtrude","CAP_FACE",FACE,{"disambiguationData":[OSD([sQuery(id+"F2.wireOp",EDGE,"E3"),sQuery(id+"F2.wireOp",EDGE,"E4"),sQuery(id+"F2.wireOp",EDGE,"E5"),sQuery(id+"F2.wireOp",EDGE,"E6"),sQuery(id+"F2.wireOp",EDGE,"E7"),sQuery(id+"F2.wireOp",EDGE,"E8"),sQuery(id+"F2.wireOp",EDGE,"E9"),sQuery(id+"F2.wireOp",EDGE,"E10"),sQuery(id+"F2.wireOp",EDGE,"E11"),sQuery(id+"F2.wireOp",EDGE,"E12"),sQuery(id+"F2.wireOp",EDGE,"E13"),sQuery(id+"F2.wireOp",EDGE,"E14")])],"isStart":true})]}),makeQuery(id+"F5.opExtrude","SWEPT_FACE",FACE,{"disambiguationData":[OSD([sQuery(id+"F4.wireOp",EDGE,"E19")])]})]});
            var Q3;
            Q3=makeQuery(id+"F5.boolean.opBoolean","INTERSECT",EDGE,{"derivedFrom":[makeQuery(id+"F3.boolean.opBoolean","MERGE",FACE,{"derivedFrom":[makeQuery(id+"F1.opExtrude","SWEPT_FACE",FACE,{"disambiguationData":[OSD([sQuery(id+"F0.wireOp",EDGE,"E0.bottom")])]}),makeQuery(id+"F3.opExtrude","CAP_FACE",FACE,{"disambiguationData":[OSD([sQuery(id+"F2.wireOp",EDGE,"E3"),sQuery(id+"F2.wireOp",EDGE,"E4"),sQuery(id+"F2.wireOp",EDGE,"E5"),sQuery(id+"F2.wireOp",EDGE,"E6"),sQuery(id+"F2.wireOp",EDGE,"E7"),sQuery(id+"F2.wireOp",EDGE,"E8"),sQuery(id+"F2.wireOp",EDGE,"E9"),sQuery(id+"F2.wireOp",EDGE,"E10"),sQuery(id+"F2.wireOp",EDGE,"E11"),sQuery(id+"F2.wireOp",EDGE,"E12"),sQuery(id+"F2.wireOp",EDGE,"E13"),sQuery(id+"F2.wireOp",EDGE,"E14")])],"isStart":true})]}),makeQuery(id+"F5.opExtrude","SWEPT_FACE",FACE,{"disambiguationData":[OSD([sQuery(id+"F4.wireOp",EDGE,"E21")])]})]});
            var Q4;
            Q4=makeQuery(id+"F3.boolean.opBoolean","MERGE",EDGE,{"derivedFrom":[makeQuery(id+"F1.opExtrude","SWEPT_EDGE",EDGE,{"disambiguationData":[OSD([sQuery(id+"F0.wireOp",EDGE,"E0.bottom"),sQuery(id+"F0.wireOp",EDGE,"E0.right")])]}),makeQuery(id+"F3.opExtrude","CAP_EDGE",EDGE,{"disambiguationData":[OSD([sQuery(id+"F2.wireOp",EDGE,"E4")])],"isStart":true})]});
            var Q5;
            {var subQ0=sQuery(id+"F0.wireOp",EDGE,"E0.top");Q5=makeQuery(id+"F3.boolean.opBoolean","MERGE",EDGE,{"derivedFrom":[makeQuery(id+"F1.opExtrude","SWEPT_EDGE",EDGE,{"disambiguationData":[OSD([subQ0,sQuery(id+"F0.wireOp",EDGE,"E0.right")])]}),makeQuery(id+"F3.opExtrude","TWEAK_EDGE",EDGE,{"derivedFrom":[makeQuery(id+"F1.opExtrude","SWEPT_FACE",FACE,{"disambiguationData":[OSD([subQ0])]}),makeQuery(id+"F2.imprint","IMPRINT",EDGE,{"derivedFrom":sQuery(id+"F2.wireOp",EDGE,"E4")})]})]});}
            var Q6;
            Q6=makeQuery(id+"F5.boolean.opBoolean","COPY",EDGE,{"derivedFrom":makeQuery(id+"F5.opExtrude","CAP_EDGE",EDGE,{"disambiguationData":[OSD([sQuery(id+"F4.wireOp",EDGE,"E21")])],"isStart":true})});
            var Q7;
            Q7=makeQuery(id+"F5.boolean.opBoolean","COPY",EDGE,{"derivedFrom":makeQuery(id+"F5.opExtrude","CAP_EDGE",EDGE,{"disambiguationData":[OSD([sQuery(id+"F4.wireOp",EDGE,"E19")])],"isStart":true})});
            var Q8;
            Q8=makeQuery(id+"F5.boolean.opBoolean","COPY",EDGE,{"derivedFrom":makeQuery(id+"F5.opExtrude","CAP_EDGE",EDGE,{"disambiguationData":[OSD([sQuery(id+"F4.wireOp",EDGE,"E17")])],"isStart":true})});
            var Q9;
            Q9=makeQuery(id+"F5.boolean.opBoolean","COPY",EDGE,{"derivedFrom":makeQuery(id+"F5.opExtrude","CAP_EDGE",EDGE,{"disambiguationData":[OSD([sQuery(id+"F4.wireOp",EDGE,"E15")])],"isStart":true})});
            var Q10;
            {var subQ0=sQuery(id+"F2.wireOp",EDGE,"E14");var subQ1=sQuery(id+"F0.wireOp",EDGE,"E0.bottom");var subQ2=makeQuery(id+"F2.imprint","INTERSECT",VERTEX,{"derivedFrom":[makeQuery(id+"F1.opExtrude","CAP_EDGE",EDGE,{"disambiguationData":[OSD([subQ1])],"isStart":true}),subQ0]});var subQ3=sQuery(id+"F0.wireOp",EDGE,"E0.left");var subQ4=sQuery(id+"F0.wireOp",EDGE,"E0.top");Q10=makeQuery(id+"F3.boolean.opBoolean","MERGE",EDGE,{"derivedFrom":[makeQuery(id+"F1.opExtrude","SWEPT_EDGE",EDGE,{"disambiguationData":[OSD([subQ4,subQ3])]}),makeQuery(id+"F3.opExtrude","TWEAK_EDGE",EDGE,{"derivedFrom":[makeQuery(id+"F1.opExtrude","SWEPT_FACE",FACE,{"disambiguationData":[OSD([subQ4])]}),makeQuery(id+"F2.imprint","IMPRINT",EDGE,{"disambiguationData":[TD([[subQ2,1.0]])],"derivedFrom":subQ0}),makeQuery(id+"F2.imprint","IMPRINT",EDGE,{"disambiguationData":[TD([[subQ2,-1.0]])],"derivedFrom":subQ0})]})]});}
            var Q11;
            Q11=makeQuery(id+"F3.boolean.opBoolean","MERGE",EDGE,{"derivedFrom":[makeQuery(id+"F1.opExtrude","SWEPT_EDGE",EDGE,{"disambiguationData":[OSD([sQuery(id+"F0.wireOp",EDGE,"E0.bottom"),sQuery(id+"F0.wireOp",EDGE,"E0.left")])]}),makeQuery(id+"F3.opExtrude","CAP_EDGE",EDGE,{"disambiguationData":[OSD([sQuery(id+"F2.wireOp",EDGE,"E14")])],"isStart":true})]});
            fillet(context, id + "F9", {"entities" : qUnion([Q0, Q1, Q2, Q3, Q4, Q5, Q6, Q7, Q8, Q9, Q10, Q11]), "radius" : 7.78 * mm, "tangentPropagation" : true, "allowEdgeOverflow" : false});
        }
        {
            var Q0;
            Q0=makeQuery(id+"F5.boolean.opBoolean","MERGE",FACE,{"derivedFrom":[makeQuery(id+"F1.opExtrude","SWEPT_FACE",FACE,{"disambiguationData":[OSD([sQuery(id+"F0.wireOp",EDGE,"E2.2.0.3")])]}),makeQuery(id+"F1.opExtrude","SWEPT_FACE",FACE,{"disambiguationData":[OSD([sQuery(id+"F0.wireOp",EDGE,"E2.2.1.3")])]}),makeQuery(id+"F1.opExtrude","SWEPT_FACE",FACE,{"disambiguationData":[OSD([sQuery(id+"F0.wireOp",EDGE,"E2.2.2.3")])]}),makeQuery(id+"F1.opExtrude","SWEPT_FACE",FACE,{"disambiguationData":[OSD([sQuery(id+"F0.wireOp",EDGE,"E2.2.3.3")])]}),makeQuery(id+"F1.opExtrude","SWEPT_FACE",FACE,{"disambiguationData":[OSD([sQuery(id+"F0.wireOp",EDGE,"E2.2.4.3")])]}),makeQuery(id+"F1.opExtrude","SWEPT_FACE",FACE,{"disambiguationData":[OSD([sQuery(id+"F0.wireOp",EDGE,"E2.2.5.3")])]}),makeQuery(id+"F1.opExtrude","SWEPT_FACE",FACE,{"disambiguationData":[OSD([sQuery(id+"F0.wireOp",EDGE,"E2.2.6.3")])]}),makeQuery(id+"F1.opExtrude","SWEPT_FACE",FACE,{"disambiguationData":[OSD([sQuery(id+"F0.wireOp",EDGE,"E2.2.7.3")])]}),makeQuery(id+"F1.opExtrude","SWEPT_FACE",FACE,{"disambiguationData":[OSD([sQuery(id+"F0.wireOp",EDGE,"E2.2.8.3")])]}),makeQuery(id+"F5.opExtrude","SWEPT_FACE",FACE,{"disambiguationData":[OSD([sQuery(id+"F4.wireOp",EDGE,"E17")])]})]});
            var sketch = newSketch(context, id + "F10", { "sketchPlane" : qUnion([Q0])});
            skLineSegment(sketch, "E28", {"start": v(6.4, 20.3) * mm, "end": v(6.4, 33) * mm});
            skLineSegment(sketch, "E29", {"start": v(6.4, 33) * mm, "end": v(7.9, 33) * mm});
            skLineSegment(sketch, "E30", {"start": v(7.9, 33) * mm, "end": v(7.9, 78.7) * mm});
            skLineSegment(sketch, "E31", {"start": v(-7.9, 78.7) * mm, "end": v(-7.9, 33) * mm});
            skLineSegment(sketch, "E32", {"start": v(-7.9, 33) * mm, "end": v(-6.4, 33) * mm});
            skLineSegment(sketch, "E33", {"start": v(-6.4, 33) * mm, "end": v(-6.4, 20.3) * mm});
            skLineSegment(sketch, "E34", {"start": v(-6.4, 20.3) * mm, "end": v(6.4, 20.3) * mm});
            skLineSegment(sketch, "E35", {"start": v(-7.9, 55.85) * mm, "end": v(7.9, 55.85) * mm, "construction": true});
            skLineSegment(sketch, "E36.MirrorCS", {"start": v(6.4, 78.7) * mm, "end": v(7.9, 78.7) * mm});
            skLineSegment(sketch, "E37.MirrorCS", {"start": v(6.4, 91.4) * mm, "end": v(6.4, 78.7) * mm});
            skLineSegment(sketch, "E38.MirrorCS", {"start": v(-6.4, 91.4) * mm, "end": v(6.4, 91.4) * mm});
            skLineSegment(sketch, "E39.MirrorCS", {"start": v(-7.9, 78.7) * mm, "end": v(-6.4, 78.7) * mm});
            skLineSegment(sketch, "E40.MirrorCS", {"start": v(-6.4, 78.7) * mm, "end": v(-6.4, 91.4) * mm});
            skSolve(sketch);
        }
        {
            var Q0;
            Q0 = qSketchRegion(id + "F10", true);
            extrude(context, id + "F11", {"entities" : qUnion([Q0]), "depth" : 13 * mm, "offsetDistance" : 25 * mm});
        }
        {
            var Q0;
            Q0=makeQuery(id+"F11.opExtrude","SWEPT_FACE",FACE,{"disambiguationData":[OSD([sQuery(id+"F10.wireOp",EDGE,"E31")])]});
            var sketch = newSketch(context, id + "F12", { "sketchPlane" : qUnion([Q0])});
            skText(sketch, "E41", { "text": "MarkerStand", "fontName": "RobotoSlab-Bold.ttf"});
            skLineSegment(sketch, "E42", {"start": v(0.07, 55.85) * mm, "end": v(0.07, 78.7) * mm, "construction": true});
            skPoint(sketch, "E42.endSnap0", {"position": v(0.07, 77.62) * mm});
            const initialGuessF12  = {"E41": [0.00257, 0.03408, 0, 1, 0.005]};
            skSetInitialGuess(sketch, initialGuessF12);
            skSolve(sketch);
        }
        {
            var Q0;
            Q0 = qSketchRegion(id + "F12", true);
            extrude(context, id + "F13", {"entities" : qUnion([Q0]), "operationType" : NewBodyOperationType.REMOVE, "oppositeDirection" : true, "depth" : 0.54 * mm, "offsetDistance" : 25 * mm});
        }
        {
            var Q0;
            Q0=makeQuery(id+"F11.opExtrude","SWEPT_FACE",FACE,{"disambiguationData":[OSD([sQuery(id+"F10.wireOp",EDGE,"E38.MirrorCS")])]});
            var sketch = newSketch(context, id + "F14", { "sketchPlane" : qUnion([Q0])});
            skText(sketch, "E43", { "text": "M", "fontName": "RobotoSlab-Bold.ttf"});
            skLineSegment(sketch, "E44", {"start": v(0, 0) * mm, "end": v(0, -5.8) * mm, "construction": true});
            const initialGuessF14  = {"E43": [0.00426, -0.0058, 0, 1, 0.00853]};
            skSetInitialGuess(sketch, initialGuessF14);
            skSolve(sketch);
        }
        {
            var Q0;
            Q0 = qSketchRegion(id + "F14", true);
            extrude(context, id + "F15", {"entities" : qUnion([Q0]), "operationType" : NewBodyOperationType.REMOVE, "oppositeDirection" : true, "depth" : 0.6 * mm, "offsetDistance" : 25 * mm});
        }
        {
            var Q0;
            Q0=makeQuery(id+"F11.opExtrude","CAP_FACE",FACE,{"disambiguationData":[OSD([sQuery(id+"F10.wireOp",EDGE,"E28"),sQuery(id+"F10.wireOp",EDGE,"E29"),sQuery(id+"F10.wireOp",EDGE,"E30"),sQuery(id+"F10.wireOp",EDGE,"E31"),sQuery(id+"F10.wireOp",EDGE,"E32"),sQuery(id+"F10.wireOp",EDGE,"E33"),sQuery(id+"F10.wireOp",EDGE,"E34"),sQuery(id+"F10.wireOp",EDGE,"E36.MirrorCS"),sQuery(id+"F10.wireOp",EDGE,"E37.MirrorCS"),sQuery(id+"F10.wireOp",EDGE,"E38.MirrorCS"),sQuery(id+"F10.wireOp",EDGE,"E39.MirrorCS"),sQuery(id+"F10.wireOp",EDGE,"E40.MirrorCS")])],"isStart":false});
            var sketch = newSketch(context, id + "F16", { "sketchPlane" : qUnion([Q0])});
            skCircle(sketch, "E45", {"center": v(-6.4, 78.7) * mm, "radius": 0.54 * mm});
            skCircle(sketch, "E46", {"center": v(6.4, 78.7) * mm, "radius": 0.54 * mm});
            skCircle(sketch, "E47", {"center": v(-6.4, 33) * mm, "radius": 0.54 * mm});
            skCircle(sketch, "E48", {"center": v(6.4, 33) * mm, "radius": 0.54 * mm});
            skSolve(sketch);
        }
        {
            var Q0;
            Q0 = qSketchRegion(id + "F16", true);
            extrude(context, id + "F17", {"entities" : qUnion([Q0]), "operationType" : NewBodyOperationType.REMOVE, "endBound" : BoundingType.THROUGH_ALL, "oppositeDirection" : true, "depth" : 25 * mm, "offsetDistance" : 25 * mm});
        }
        {
            var Q0;
            Q0=makeQuery(id+"F11.opExtrude","SWEPT_EDGE",EDGE,{"disambiguationData":[OSD([sQuery(id+"F10.wireOp",EDGE,"E31"),sQuery(id+"F10.wireOp",EDGE,"E39.MirrorCS")])]});
            var Q1;
            Q1=makeQuery(id+"F17.boolean.opBoolean","INTERSECT",EDGE,{"derivedFrom":[makeQuery(id+"F11.opExtrude","SWEPT_FACE",FACE,{"disambiguationData":[OSD([sQuery(id+"F10.wireOp",EDGE,"E39.MirrorCS")])]}),makeQuery(id+"F17.opExtrude","SWEPT_FACE",FACE,{"disambiguationData":[OSD([sQuery(id+"F16.wireOp",EDGE,"E45")])]})]});
            var Q2;
            Q2=makeQuery(id+"F17.boolean.opBoolean","INTERSECT",EDGE,{"derivedFrom":[makeQuery(id+"F11.opExtrude","SWEPT_FACE",FACE,{"disambiguationData":[OSD([sQuery(id+"F10.wireOp",EDGE,"E40.MirrorCS")])]}),makeQuery(id+"F17.opExtrude","SWEPT_FACE",FACE,{"disambiguationData":[OSD([sQuery(id+"F16.wireOp",EDGE,"E45")])]})]});
            var Q3;
            Q3=makeQuery(id+"F17.boolean.opBoolean","INTERSECT",EDGE,{"derivedFrom":[makeQuery(id+"F11.opExtrude","SWEPT_FACE",FACE,{"disambiguationData":[OSD([sQuery(id+"F10.wireOp",EDGE,"E36.MirrorCS")])]}),makeQuery(id+"F17.opExtrude","SWEPT_FACE",FACE,{"disambiguationData":[OSD([sQuery(id+"F16.wireOp",EDGE,"E46")])]})]});
            var Q4;
            Q4=makeQuery(id+"F11.opExtrude","SWEPT_EDGE",EDGE,{"disambiguationData":[OSD([sQuery(id+"F10.wireOp",EDGE,"E30"),sQuery(id+"F10.wireOp",EDGE,"E36.MirrorCS")])]});
            var Q5;
            Q5=makeQuery(id+"F11.opExtrude","SWEPT_EDGE",EDGE,{"disambiguationData":[OSD([sQuery(id+"F10.wireOp",EDGE,"E37.MirrorCS"),sQuery(id+"F10.wireOp",EDGE,"E38.MirrorCS")])]});
            var Q6;
            Q6=makeQuery(id+"F11.opExtrude","SWEPT_EDGE",EDGE,{"disambiguationData":[OSD([sQuery(id+"F10.wireOp",EDGE,"E38.MirrorCS"),sQuery(id+"F10.wireOp",EDGE,"E40.MirrorCS")])]});
            var Q7;
            Q7=makeQuery(id+"F17.boolean.opBoolean","INTERSECT",EDGE,{"derivedFrom":[makeQuery(id+"F11.opExtrude","SWEPT_FACE",FACE,{"disambiguationData":[OSD([sQuery(id+"F10.wireOp",EDGE,"E37.MirrorCS")])]}),makeQuery(id+"F17.opExtrude","SWEPT_FACE",FACE,{"disambiguationData":[OSD([sQuery(id+"F16.wireOp",EDGE,"E46")])]})]});
            var Q8;
            Q8=makeQuery(id+"F11.opExtrude","SWEPT_EDGE",EDGE,{"disambiguationData":[OSD([sQuery(id+"F10.wireOp",EDGE,"E29"),sQuery(id+"F10.wireOp",EDGE,"E30")])]});
            var Q9;
            Q9=makeQuery(id+"F17.boolean.opBoolean","INTERSECT",EDGE,{"derivedFrom":[makeQuery(id+"F11.opExtrude","SWEPT_FACE",FACE,{"disambiguationData":[OSD([sQuery(id+"F10.wireOp",EDGE,"E28")])]}),makeQuery(id+"F17.opExtrude","SWEPT_FACE",FACE,{"disambiguationData":[OSD([sQuery(id+"F16.wireOp",EDGE,"E48")])]})]});
            var Q10;
            Q10=makeQuery(id+"F11.opExtrude","SWEPT_EDGE",EDGE,{"disambiguationData":[OSD([sQuery(id+"F10.wireOp",EDGE,"E28"),sQuery(id+"F10.wireOp",EDGE,"E34")])]});
            var Q11;
            Q11=makeQuery(id+"F17.boolean.opBoolean","INTERSECT",EDGE,{"derivedFrom":[makeQuery(id+"F11.opExtrude","SWEPT_FACE",FACE,{"disambiguationData":[OSD([sQuery(id+"F10.wireOp",EDGE,"E29")])]}),makeQuery(id+"F17.opExtrude","SWEPT_FACE",FACE,{"disambiguationData":[OSD([sQuery(id+"F16.wireOp",EDGE,"E48")])]})]});
            var Q12;
            Q12=makeQuery(id+"F17.boolean.opBoolean","INTERSECT",EDGE,{"derivedFrom":[makeQuery(id+"F11.opExtrude","SWEPT_FACE",FACE,{"disambiguationData":[OSD([sQuery(id+"F10.wireOp",EDGE,"E32")])]}),makeQuery(id+"F17.opExtrude","SWEPT_FACE",FACE,{"disambiguationData":[OSD([sQuery(id+"F16.wireOp",EDGE,"E47")])]})]});
            var Q13;
            Q13=makeQuery(id+"F11.opExtrude","SWEPT_EDGE",EDGE,{"disambiguationData":[OSD([sQuery(id+"F10.wireOp",EDGE,"E31"),sQuery(id+"F10.wireOp",EDGE,"E32")])]});
            var Q14;
            Q14=makeQuery(id+"F11.opExtrude","SWEPT_EDGE",EDGE,{"disambiguationData":[OSD([sQuery(id+"F10.wireOp",EDGE,"E33"),sQuery(id+"F10.wireOp",EDGE,"E34")])]});
            var Q15;
            Q15=makeQuery(id+"F17.boolean.opBoolean","INTERSECT",EDGE,{"derivedFrom":[makeQuery(id+"F11.opExtrude","SWEPT_FACE",FACE,{"disambiguationData":[OSD([sQuery(id+"F10.wireOp",EDGE,"E33")])]}),makeQuery(id+"F17.opExtrude","SWEPT_FACE",FACE,{"disambiguationData":[OSD([sQuery(id+"F16.wireOp",EDGE,"E47")])]})]});
            fillet(context, id + "F18", {"entities" : qUnion([Q0, Q1, Q2, Q3, Q4, Q5, Q6, Q7, Q8, Q9, Q10, Q11, Q12, Q13, Q14, Q15]), "radius" : 0.54 * mm, "tangentPropagation" : true, "allowEdgeOverflow" : false});
        }
        {
            var Q0;
            Q0=makeQuery(id+"F11.opExtrude","SWEPT_FACE",FACE,{"disambiguationData":[OSD([sQuery(id+"F10.wireOp",EDGE,"E38.MirrorCS")])]});
            var sketch = newSketch(context, id + "F19", { "sketchPlane" : qUnion([Q0])});
            skLineSegment(sketch, "E49.bottom", {"start": v(-37.1, 66.3) * mm, "end": v(37.1, 66.3) * mm});
            skLineSegment(sketch, "E49.top", {"start": v(-37.1, -66.3) * mm, "end": v(37.1, -66.3) * mm});
            skLineSegment(sketch, "E49.left", {"start": v(-37.1, 66.3) * mm, "end": v(-37.1, -66.3) * mm});
            skLineSegment(sketch, "E49.right", {"start": v(37.1, 66.3) * mm, "end": v(37.1, -66.3) * mm});
            skPoint(sketch, "E49.middle", {"position": v(0, 0) * mm});
            skLineSegment(sketch, "E50.bottom", {"start": v(-22.5, 51.7) * mm, "end": v(-35.9, 51.7) * mm});
            skLineSegment(sketch, "E50.top", {"start": v(-22.5, 65.1) * mm, "end": v(-35.9, 65.1) * mm});
            skLineSegment(sketch, "E50.left", {"start": v(-22.5, 51.7) * mm, "end": v(-22.5, 65.1) * mm});
            skLineSegment(sketch, "E50.right", {"start": v(-35.9, 51.7) * mm, "end": v(-35.9, 65.1) * mm});
            skLineSegment(sketch, "E51.0.1.0", {"start": v(-35.9, 37.1) * mm, "end": v(-35.9, 50.5) * mm});
            skLineSegment(sketch, "E51.0.1.1", {"start": v(-22.5, 37.1) * mm, "end": v(-35.9, 37.1) * mm});
            skLineSegment(sketch, "E51.0.1.2", {"start": v(-22.5, 37.1) * mm, "end": v(-22.5, 50.5) * mm});
            skLineSegment(sketch, "E51.0.1.3", {"start": v(-22.5, 50.5) * mm, "end": v(-35.9, 50.5) * mm});
            skLineSegment(sketch, "E51.0.2.0", {"start": v(-35.9, 22.5) * mm, "end": v(-35.9, 35.9) * mm});
            skLineSegment(sketch, "E51.0.2.1", {"start": v(-22.5, 22.5) * mm, "end": v(-35.9, 22.5) * mm});
            skLineSegment(sketch, "E51.0.2.2", {"start": v(-22.5, 22.5) * mm, "end": v(-22.5, 35.9) * mm});
            skLineSegment(sketch, "E51.0.2.3", {"start": v(-22.5, 35.9) * mm, "end": v(-35.9, 35.9) * mm});
            skLineSegment(sketch, "E51.0.3.0", {"start": v(-35.9, 7.9) * mm, "end": v(-35.9, 21.3) * mm});
            skLineSegment(sketch, "E51.0.3.1", {"start": v(-22.5, 7.9) * mm, "end": v(-35.9, 7.9) * mm});
            skLineSegment(sketch, "E51.0.3.2", {"start": v(-22.5, 7.9) * mm, "end": v(-22.5, 21.3) * mm});
            skLineSegment(sketch, "E51.0.3.3", {"start": v(-22.5, 21.3) * mm, "end": v(-35.9, 21.3) * mm});
            skLineSegment(sketch, "E51.0.4.0", {"start": v(-35.9, -6.7) * mm, "end": v(-35.9, 6.7) * mm});
            skLineSegment(sketch, "E51.0.4.1", {"start": v(-22.5, -6.7) * mm, "end": v(-35.9, -6.7) * mm});
            skLineSegment(sketch, "E51.0.4.2", {"start": v(-22.5, -6.7) * mm, "end": v(-22.5, 6.7) * mm});
            skLineSegment(sketch, "E51.0.4.3", {"start": v(-22.5, 6.7) * mm, "end": v(-35.9, 6.7) * mm});
            skLineSegment(sketch, "E51.0.5.0", {"start": v(-35.9, -21.3) * mm, "end": v(-35.9, -7.9) * mm});
            skLineSegment(sketch, "E51.0.5.1", {"start": v(-22.5, -21.3) * mm, "end": v(-35.9, -21.3) * mm});
            skLineSegment(sketch, "E51.0.5.2", {"start": v(-22.5, -21.3) * mm, "end": v(-22.5, -7.9) * mm});
            skLineSegment(sketch, "E51.0.5.3", {"start": v(-22.5, -7.9) * mm, "end": v(-35.9, -7.9) * mm});
            skLineSegment(sketch, "E51.0.6.0", {"start": v(-35.9, -35.9) * mm, "end": v(-35.9, -22.5) * mm});
            skLineSegment(sketch, "E51.0.6.1", {"start": v(-22.5, -35.9) * mm, "end": v(-35.9, -35.9) * mm});
            skLineSegment(sketch, "E51.0.6.2", {"start": v(-22.5, -35.9) * mm, "end": v(-22.5, -22.5) * mm});
            skLineSegment(sketch, "E51.0.6.3", {"start": v(-22.5, -22.5) * mm, "end": v(-35.9, -22.5) * mm});
            skLineSegment(sketch, "E51.0.7.0", {"start": v(-35.9, -50.5) * mm, "end": v(-35.9, -37.1) * mm});
            skLineSegment(sketch, "E51.0.7.1", {"start": v(-22.5, -50.5) * mm, "end": v(-35.9, -50.5) * mm});
            skLineSegment(sketch, "E51.0.7.2", {"start": v(-22.5, -50.5) * mm, "end": v(-22.5, -37.1) * mm});
            skLineSegment(sketch, "E51.0.7.3", {"start": v(-22.5, -37.1) * mm, "end": v(-35.9, -37.1) * mm});
            skLineSegment(sketch, "E51.0.8.0", {"start": v(-35.9, -65.1) * mm, "end": v(-35.9, -51.7) * mm});
            skLineSegment(sketch, "E51.0.8.1", {"start": v(-22.5, -65.1) * mm, "end": v(-35.9, -65.1) * mm});
            skLineSegment(sketch, "E51.0.8.2", {"start": v(-22.5, -65.1) * mm, "end": v(-22.5, -51.7) * mm});
            skLineSegment(sketch, "E51.0.8.3", {"start": v(-22.5, -51.7) * mm, "end": v(-35.9, -51.7) * mm});
            skLineSegment(sketch, "E51.1.0.0", {"start": v(-21.3, 51.7) * mm, "end": v(-21.3, 65.1) * mm});
            skLineSegment(sketch, "E51.1.0.1", {"start": v(-7.9, 51.7) * mm, "end": v(-21.3, 51.7) * mm});
            skLineSegment(sketch, "E51.1.0.2", {"start": v(-7.9, 51.7) * mm, "end": v(-7.9, 65.1) * mm});
            skLineSegment(sketch, "E51.1.0.3", {"start": v(-7.9, 65.1) * mm, "end": v(-21.3, 65.1) * mm});
            skLineSegment(sketch, "E51.1.1.0", {"start": v(-21.3, 37.1) * mm, "end": v(-21.3, 50.5) * mm});
            skLineSegment(sketch, "E51.1.1.1", {"start": v(-7.9, 37.1) * mm, "end": v(-21.3, 37.1) * mm});
            skLineSegment(sketch, "E51.1.1.2", {"start": v(-7.9, 37.1) * mm, "end": v(-7.9, 50.5) * mm});
            skLineSegment(sketch, "E51.1.1.3", {"start": v(-7.9, 50.5) * mm, "end": v(-21.3, 50.5) * mm});
            skLineSegment(sketch, "E51.1.2.0", {"start": v(-21.3, 22.5) * mm, "end": v(-21.3, 35.9) * mm});
            skLineSegment(sketch, "E51.1.2.1", {"start": v(-7.9, 22.5) * mm, "end": v(-21.3, 22.5) * mm});
            skLineSegment(sketch, "E51.1.2.2", {"start": v(-7.9, 22.5) * mm, "end": v(-7.9, 35.9) * mm});
            skLineSegment(sketch, "E51.1.2.3", {"start": v(-7.9, 35.9) * mm, "end": v(-21.3, 35.9) * mm});
            skLineSegment(sketch, "E51.1.3.0", {"start": v(-21.3, 7.9) * mm, "end": v(-21.3, 21.3) * mm});
            skLineSegment(sketch, "E51.1.3.1", {"start": v(-7.9, 7.9) * mm, "end": v(-21.3, 7.9) * mm});
            skLineSegment(sketch, "E51.1.3.2", {"start": v(-7.9, 7.9) * mm, "end": v(-7.9, 21.3) * mm});
            skLineSegment(sketch, "E51.1.3.3", {"start": v(-7.9, 21.3) * mm, "end": v(-21.3, 21.3) * mm});
            skLineSegment(sketch, "E51.1.4.0", {"start": v(-21.3, -6.7) * mm, "end": v(-21.3, 6.7) * mm});
            skLineSegment(sketch, "E51.1.4.1", {"start": v(-7.9, -6.7) * mm, "end": v(-21.3, -6.7) * mm});
            skLineSegment(sketch, "E51.1.4.2", {"start": v(-7.9, -6.7) * mm, "end": v(-7.9, 6.7) * mm});
            skLineSegment(sketch, "E51.1.4.3", {"start": v(-7.9, 6.7) * mm, "end": v(-21.3, 6.7) * mm});
            skLineSegment(sketch, "E51.1.5.0", {"start": v(-21.3, -21.3) * mm, "end": v(-21.3, -7.9) * mm});
            skLineSegment(sketch, "E51.1.5.1", {"start": v(-7.9, -21.3) * mm, "end": v(-21.3, -21.3) * mm});
            skLineSegment(sketch, "E51.1.5.2", {"start": v(-7.9, -21.3) * mm, "end": v(-7.9, -7.9) * mm});
            skLineSegment(sketch, "E51.1.5.3", {"start": v(-7.9, -7.9) * mm, "end": v(-21.3, -7.9) * mm});
            skLineSegment(sketch, "E51.1.6.0", {"start": v(-21.3, -35.9) * mm, "end": v(-21.3, -22.5) * mm});
            skLineSegment(sketch, "E51.1.6.1", {"start": v(-7.9, -35.9) * mm, "end": v(-21.3, -35.9) * mm});
            skLineSegment(sketch, "E51.1.6.2", {"start": v(-7.9, -35.9) * mm, "end": v(-7.9, -22.5) * mm});
            skLineSegment(sketch, "E51.1.6.3", {"start": v(-7.9, -22.5) * mm, "end": v(-21.3, -22.5) * mm});
            skLineSegment(sketch, "E51.1.7.0", {"start": v(-21.3, -50.5) * mm, "end": v(-21.3, -37.1) * mm});
            skLineSegment(sketch, "E51.1.7.1", {"start": v(-7.9, -50.5) * mm, "end": v(-21.3, -50.5) * mm});
            skLineSegment(sketch, "E51.1.7.2", {"start": v(-7.9, -50.5) * mm, "end": v(-7.9, -37.1) * mm});
            skLineSegment(sketch, "E51.1.7.3", {"start": v(-7.9, -37.1) * mm, "end": v(-21.3, -37.1) * mm});
            skLineSegment(sketch, "E51.1.8.0", {"start": v(-21.3, -65.1) * mm, "end": v(-21.3, -51.7) * mm});
            skLineSegment(sketch, "E51.1.8.1", {"start": v(-7.9, -65.1) * mm, "end": v(-21.3, -65.1) * mm});
            skLineSegment(sketch, "E51.1.8.2", {"start": v(-7.9, -65.1) * mm, "end": v(-7.9, -51.7) * mm});
            skLineSegment(sketch, "E51.1.8.3", {"start": v(-7.9, -51.7) * mm, "end": v(-21.3, -51.7) * mm});
            skLineSegment(sketch, "E51.2.0.0", {"start": v(-6.7, 51.7) * mm, "end": v(-6.7, 65.1) * mm});
            skLineSegment(sketch, "E51.2.0.1", {"start": v(6.7, 51.7) * mm, "end": v(-6.7, 51.7) * mm});
            skLineSegment(sketch, "E51.2.0.2", {"start": v(6.7, 51.7) * mm, "end": v(6.7, 65.1) * mm});
            skLineSegment(sketch, "E51.2.0.3", {"start": v(6.7, 65.1) * mm, "end": v(-6.7, 65.1) * mm});
            skLineSegment(sketch, "E51.2.1.0", {"start": v(-6.7, 37.1) * mm, "end": v(-6.7, 50.5) * mm});
            skLineSegment(sketch, "E51.2.1.1", {"start": v(6.7, 37.1) * mm, "end": v(-6.7, 37.1) * mm});
            skLineSegment(sketch, "E51.2.1.2", {"start": v(6.7, 37.1) * mm, "end": v(6.7, 50.5) * mm});
            skLineSegment(sketch, "E51.2.1.3", {"start": v(6.7, 50.5) * mm, "end": v(-6.7, 50.5) * mm});
            skLineSegment(sketch, "E51.2.2.0", {"start": v(-6.7, 22.5) * mm, "end": v(-6.7, 35.9) * mm});
            skLineSegment(sketch, "E51.2.2.1", {"start": v(6.7, 22.5) * mm, "end": v(-6.7, 22.5) * mm});
            skLineSegment(sketch, "E51.2.2.2", {"start": v(6.7, 22.5) * mm, "end": v(6.7, 35.9) * mm});
            skLineSegment(sketch, "E51.2.2.3", {"start": v(6.7, 35.9) * mm, "end": v(-6.7, 35.9) * mm});
            skLineSegment(sketch, "E51.2.3.0", {"start": v(-6.7, 7.9) * mm, "end": v(-6.7, 21.3) * mm});
            skLineSegment(sketch, "E51.2.3.1", {"start": v(6.7, 7.9) * mm, "end": v(-6.7, 7.9) * mm});
            skLineSegment(sketch, "E51.2.3.2", {"start": v(6.7, 7.9) * mm, "end": v(6.7, 21.3) * mm});
            skLineSegment(sketch, "E51.2.3.3", {"start": v(6.7, 21.3) * mm, "end": v(-6.7, 21.3) * mm});
            skLineSegment(sketch, "E51.2.4.0", {"start": v(-6.7, -6.7) * mm, "end": v(-6.7, 6.7) * mm});
            skLineSegment(sketch, "E51.2.4.1", {"start": v(6.7, -6.7) * mm, "end": v(-6.7, -6.7) * mm});
            skLineSegment(sketch, "E51.2.4.2", {"start": v(6.7, -6.7) * mm, "end": v(6.7, 6.7) * mm});
            skLineSegment(sketch, "E51.2.4.3", {"start": v(6.7, 6.7) * mm, "end": v(-6.7, 6.7) * mm});
            skLineSegment(sketch, "E51.2.5.0", {"start": v(-6.7, -21.3) * mm, "end": v(-6.7, -7.9) * mm});
            skLineSegment(sketch, "E51.2.5.1", {"start": v(6.7, -21.3) * mm, "end": v(-6.7, -21.3) * mm});
            skLineSegment(sketch, "E51.2.5.2", {"start": v(6.7, -21.3) * mm, "end": v(6.7, -7.9) * mm});
            skLineSegment(sketch, "E51.2.5.3", {"start": v(6.7, -7.9) * mm, "end": v(-6.7, -7.9) * mm});
            skLineSegment(sketch, "E51.2.6.0", {"start": v(-6.7, -35.9) * mm, "end": v(-6.7, -22.5) * mm});
            skLineSegment(sketch, "E51.2.6.1", {"start": v(6.7, -35.9) * mm, "end": v(-6.7, -35.9) * mm});
            skLineSegment(sketch, "E51.2.6.2", {"start": v(6.7, -35.9) * mm, "end": v(6.7, -22.5) * mm});
            skLineSegment(sketch, "E51.2.6.3", {"start": v(6.7, -22.5) * mm, "end": v(-6.7, -22.5) * mm});
            skLineSegment(sketch, "E51.2.7.0", {"start": v(-6.7, -50.5) * mm, "end": v(-6.7, -37.1) * mm});
            skLineSegment(sketch, "E51.2.7.1", {"start": v(6.7, -50.5) * mm, "end": v(-6.7, -50.5) * mm});
            skLineSegment(sketch, "E51.2.7.2", {"start": v(6.7, -50.5) * mm, "end": v(6.7, -37.1) * mm});
            skLineSegment(sketch, "E51.2.7.3", {"start": v(6.7, -37.1) * mm, "end": v(-6.7, -37.1) * mm});
            skLineSegment(sketch, "E51.2.8.0", {"start": v(-6.7, -65.1) * mm, "end": v(-6.7, -51.7) * mm});
            skLineSegment(sketch, "E51.2.8.1", {"start": v(6.7, -65.1) * mm, "end": v(-6.7, -65.1) * mm});
            skLineSegment(sketch, "E51.2.8.2", {"start": v(6.7, -65.1) * mm, "end": v(6.7, -51.7) * mm});
            skLineSegment(sketch, "E51.2.8.3", {"start": v(6.7, -51.7) * mm, "end": v(-6.7, -51.7) * mm});
            skLineSegment(sketch, "E51.3.0.0", {"start": v(7.9, 51.7) * mm, "end": v(7.9, 65.1) * mm});
            skLineSegment(sketch, "E51.3.0.1", {"start": v(21.3, 51.7) * mm, "end": v(7.9, 51.7) * mm});
            skLineSegment(sketch, "E51.3.0.2", {"start": v(21.3, 51.7) * mm, "end": v(21.3, 65.1) * mm});
            skLineSegment(sketch, "E51.3.0.3", {"start": v(21.3, 65.1) * mm, "end": v(7.9, 65.1) * mm});
            skLineSegment(sketch, "E51.3.1.0", {"start": v(7.9, 37.1) * mm, "end": v(7.9, 50.5) * mm});
            skLineSegment(sketch, "E51.3.1.1", {"start": v(21.3, 37.1) * mm, "end": v(7.9, 37.1) * mm});
            skLineSegment(sketch, "E51.3.1.2", {"start": v(21.3, 37.1) * mm, "end": v(21.3, 50.5) * mm});
            skLineSegment(sketch, "E51.3.1.3", {"start": v(21.3, 50.5) * mm, "end": v(7.9, 50.5) * mm});
            skLineSegment(sketch, "E51.3.2.0", {"start": v(7.9, 22.5) * mm, "end": v(7.9, 35.9) * mm});
            skLineSegment(sketch, "E51.3.2.1", {"start": v(21.3, 22.5) * mm, "end": v(7.9, 22.5) * mm});
            skLineSegment(sketch, "E51.3.2.2", {"start": v(21.3, 22.5) * mm, "end": v(21.3, 35.9) * mm});
            skLineSegment(sketch, "E51.3.2.3", {"start": v(21.3, 35.9) * mm, "end": v(7.9, 35.9) * mm});
            skLineSegment(sketch, "E51.3.3.0", {"start": v(7.9, 7.9) * mm, "end": v(7.9, 21.3) * mm});
            skLineSegment(sketch, "E51.3.3.1", {"start": v(21.3, 7.9) * mm, "end": v(7.9, 7.9) * mm});
            skLineSegment(sketch, "E51.3.3.2", {"start": v(21.3, 7.9) * mm, "end": v(21.3, 21.3) * mm});
            skLineSegment(sketch, "E51.3.3.3", {"start": v(21.3, 21.3) * mm, "end": v(7.9, 21.3) * mm});
            skLineSegment(sketch, "E51.3.4.0", {"start": v(7.9, -6.7) * mm, "end": v(7.9, 6.7) * mm});
            skLineSegment(sketch, "E51.3.4.1", {"start": v(21.3, -6.7) * mm, "end": v(7.9, -6.7) * mm});
            skLineSegment(sketch, "E51.3.4.2", {"start": v(21.3, -6.7) * mm, "end": v(21.3, 6.7) * mm});
            skLineSegment(sketch, "E51.3.4.3", {"start": v(21.3, 6.7) * mm, "end": v(7.9, 6.7) * mm});
            skLineSegment(sketch, "E51.3.5.0", {"start": v(7.9, -21.3) * mm, "end": v(7.9, -7.9) * mm});
            skLineSegment(sketch, "E51.3.5.1", {"start": v(21.3, -21.3) * mm, "end": v(7.9, -21.3) * mm});
            skLineSegment(sketch, "E51.3.5.2", {"start": v(21.3, -21.3) * mm, "end": v(21.3, -7.9) * mm});
            skLineSegment(sketch, "E51.3.5.3", {"start": v(21.3, -7.9) * mm, "end": v(7.9, -7.9) * mm});
            skLineSegment(sketch, "E51.3.6.0", {"start": v(7.9, -35.9) * mm, "end": v(7.9, -22.5) * mm});
            skLineSegment(sketch, "E51.3.6.1", {"start": v(21.3, -35.9) * mm, "end": v(7.9, -35.9) * mm});
            skLineSegment(sketch, "E51.3.6.2", {"start": v(21.3, -35.9) * mm, "end": v(21.3, -22.5) * mm});
            skLineSegment(sketch, "E51.3.6.3", {"start": v(21.3, -22.5) * mm, "end": v(7.9, -22.5) * mm});
            skLineSegment(sketch, "E51.3.7.0", {"start": v(7.9, -50.5) * mm, "end": v(7.9, -37.1) * mm});
            skLineSegment(sketch, "E51.3.7.1", {"start": v(21.3, -50.5) * mm, "end": v(7.9, -50.5) * mm});
            skLineSegment(sketch, "E51.3.7.2", {"start": v(21.3, -50.5) * mm, "end": v(21.3, -37.1) * mm});
            skLineSegment(sketch, "E51.3.7.3", {"start": v(21.3, -37.1) * mm, "end": v(7.9, -37.1) * mm});
            skLineSegment(sketch, "E51.3.8.0", {"start": v(7.9, -65.1) * mm, "end": v(7.9, -51.7) * mm});
            skLineSegment(sketch, "E51.3.8.1", {"start": v(21.3, -65.1) * mm, "end": v(7.9, -65.1) * mm});
            skLineSegment(sketch, "E51.3.8.2", {"start": v(21.3, -65.1) * mm, "end": v(21.3, -51.7) * mm});
            skLineSegment(sketch, "E51.3.8.3", {"start": v(21.3, -51.7) * mm, "end": v(7.9, -51.7) * mm});
            skLineSegment(sketch, "E51.4.0.0", {"start": v(22.5, 51.7) * mm, "end": v(22.5, 65.1) * mm});
            skLineSegment(sketch, "E51.4.0.1", {"start": v(35.9, 51.7) * mm, "end": v(22.5, 51.7) * mm});
            skLineSegment(sketch, "E51.4.0.2", {"start": v(35.9, 51.7) * mm, "end": v(35.9, 65.1) * mm});
            skLineSegment(sketch, "E51.4.0.3", {"start": v(35.9, 65.1) * mm, "end": v(22.5, 65.1) * mm});
            skLineSegment(sketch, "E51.4.1.0", {"start": v(22.5, 37.1) * mm, "end": v(22.5, 50.5) * mm});
            skLineSegment(sketch, "E51.4.1.1", {"start": v(35.9, 37.1) * mm, "end": v(22.5, 37.1) * mm});
            skLineSegment(sketch, "E51.4.1.2", {"start": v(35.9, 37.1) * mm, "end": v(35.9, 50.5) * mm});
            skLineSegment(sketch, "E51.4.1.3", {"start": v(35.9, 50.5) * mm, "end": v(22.5, 50.5) * mm});
            skLineSegment(sketch, "E51.4.2.0", {"start": v(22.5, 22.5) * mm, "end": v(22.5, 35.9) * mm});
            skLineSegment(sketch, "E51.4.2.1", {"start": v(35.9, 22.5) * mm, "end": v(22.5, 22.5) * mm});
            skLineSegment(sketch, "E51.4.2.2", {"start": v(35.9, 22.5) * mm, "end": v(35.9, 35.9) * mm});
            skLineSegment(sketch, "E51.4.2.3", {"start": v(35.9, 35.9) * mm, "end": v(22.5, 35.9) * mm});
            skLineSegment(sketch, "E51.4.3.0", {"start": v(22.5, 7.9) * mm, "end": v(22.5, 21.3) * mm});
            skLineSegment(sketch, "E51.4.3.1", {"start": v(35.9, 7.9) * mm, "end": v(22.5, 7.9) * mm});
            skLineSegment(sketch, "E51.4.3.2", {"start": v(35.9, 7.9) * mm, "end": v(35.9, 21.3) * mm});
            skLineSegment(sketch, "E51.4.3.3", {"start": v(35.9, 21.3) * mm, "end": v(22.5, 21.3) * mm});
            skLineSegment(sketch, "E51.4.4.0", {"start": v(22.5, -6.7) * mm, "end": v(22.5, 6.7) * mm});
            skLineSegment(sketch, "E51.4.4.1", {"start": v(35.9, -6.7) * mm, "end": v(22.5, -6.7) * mm});
            skLineSegment(sketch, "E51.4.4.2", {"start": v(35.9, -6.7) * mm, "end": v(35.9, 6.7) * mm});
            skLineSegment(sketch, "E51.4.4.3", {"start": v(35.9, 6.7) * mm, "end": v(22.5, 6.7) * mm});
            skLineSegment(sketch, "E51.4.5.0", {"start": v(22.5, -21.3) * mm, "end": v(22.5, -7.9) * mm});
            skLineSegment(sketch, "E51.4.5.1", {"start": v(35.9, -21.3) * mm, "end": v(22.5, -21.3) * mm});
            skLineSegment(sketch, "E51.4.5.2", {"start": v(35.9, -21.3) * mm, "end": v(35.9, -7.9) * mm});
            skLineSegment(sketch, "E51.4.5.3", {"start": v(35.9, -7.9) * mm, "end": v(22.5, -7.9) * mm});
            skLineSegment(sketch, "E51.4.6.0", {"start": v(22.5, -35.9) * mm, "end": v(22.5, -22.5) * mm});
            skLineSegment(sketch, "E51.4.6.1", {"start": v(35.9, -35.9) * mm, "end": v(22.5, -35.9) * mm});
            skLineSegment(sketch, "E51.4.6.2", {"start": v(35.9, -35.9) * mm, "end": v(35.9, -22.5) * mm});
            skLineSegment(sketch, "E51.4.6.3", {"start": v(35.9, -22.5) * mm, "end": v(22.5, -22.5) * mm});
            skLineSegment(sketch, "E51.4.7.0", {"start": v(22.5, -50.5) * mm, "end": v(22.5, -37.1) * mm});
            skLineSegment(sketch, "E51.4.7.1", {"start": v(35.9, -50.5) * mm, "end": v(22.5, -50.5) * mm});
            skLineSegment(sketch, "E51.4.7.2", {"start": v(35.9, -50.5) * mm, "end": v(35.9, -37.1) * mm});
            skLineSegment(sketch, "E51.4.7.3", {"start": v(35.9, -37.1) * mm, "end": v(22.5, -37.1) * mm});
            skLineSegment(sketch, "E51.4.8.0", {"start": v(22.5, -65.1) * mm, "end": v(22.5, -51.7) * mm});
            skLineSegment(sketch, "E51.4.8.1", {"start": v(35.9, -65.1) * mm, "end": v(22.5, -65.1) * mm});
            skLineSegment(sketch, "E51.4.8.2", {"start": v(35.9, -65.1) * mm, "end": v(35.9, -51.7) * mm});
            skLineSegment(sketch, "E51.4.8.3", {"start": v(35.9, -51.7) * mm, "end": v(22.5, -51.7) * mm});
            skLineSegment(sketch, "E51.direction1", {"start": v(-35.9, 51.7) * mm, "end": v(-21.3, 51.7) * mm, "construction": true});
            skLineSegment(sketch, "E51.direction2", {"start": v(-35.9, 51.7) * mm, "end": v(-35.9, 37.1) * mm, "construction": true});
            skSolve(sketch);
        }
        {
            var Q0;
            Q0 = qSketchRegion(id + "F19", true);
            extrude(context, id + "F20", {"entities" : qUnion([Q0]), "oppositeDirection" : true, "depth" : 13 * mm, "offsetDistance" : 25 * mm});
        }
        {
            var Q0;
            Q0=makeQuery(id+"F20.opExtrude","SWEPT_EDGE",EDGE,{"disambiguationData":[OSD([sQuery(id+"F19.wireOp",EDGE,"E50.top"),sQuery(id+"F19.wireOp",EDGE,"E50.right")])]});
            var Q1;
            Q1=makeQuery(id+"F20.opExtrude","SWEPT_EDGE",EDGE,{"disambiguationData":[OSD([sQuery(id+"F19.wireOp",EDGE,"E51.0.8.0"),sQuery(id+"F19.wireOp",EDGE,"E51.0.8.1")])]});
            var Q2;
            Q2=makeQuery(id+"F20.opExtrude","SWEPT_EDGE",EDGE,{"disambiguationData":[OSD([sQuery(id+"F19.wireOp",EDGE,"E51.4.0.2"),sQuery(id+"F19.wireOp",EDGE,"E51.4.0.3")])]});
            var Q3;
            Q3=makeQuery(id+"F20.opExtrude","SWEPT_EDGE",EDGE,{"disambiguationData":[OSD([sQuery(id+"F19.wireOp",EDGE,"E51.4.8.1"),sQuery(id+"F19.wireOp",EDGE,"E51.4.8.2")])]});
            fillet(context, id + "F21", {"entities" : qUnion([Q0, Q1, Q2, Q3]), "radius" : 6.7 * mm, "tangentPropagation" : true, "allowEdgeOverflow" : false});
        }
        {
            var Q0;
            Q0=makeQuery(id+"F20.opExtrude","SWEPT_EDGE",EDGE,{"disambiguationData":[OSD([sQuery(id+"F19.wireOp",EDGE,"E49.bottom"),sQuery(id+"F19.wireOp",EDGE,"E49.left")])]});
            var Q1;
            Q1=makeQuery(id+"F20.opExtrude","SWEPT_EDGE",EDGE,{"disambiguationData":[OSD([sQuery(id+"F19.wireOp",EDGE,"E49.bottom"),sQuery(id+"F19.wireOp",EDGE,"E49.right")])]});
            var Q2;
            Q2=makeQuery(id+"F20.opExtrude","SWEPT_EDGE",EDGE,{"disambiguationData":[OSD([sQuery(id+"F19.wireOp",EDGE,"E49.top"),sQuery(id+"F19.wireOp",EDGE,"E49.left")])]});
            var Q3;
            Q3=makeQuery(id+"F20.opExtrude","SWEPT_EDGE",EDGE,{"disambiguationData":[OSD([sQuery(id+"F19.wireOp",EDGE,"E49.top"),sQuery(id+"F19.wireOp",EDGE,"E49.right")])]});
            fillet(context, id + "F22", {"entities" : qUnion([Q0, Q1, Q2, Q3]), "radius" : 7.78 * mm, "tangentPropagation" : true, "allowEdgeOverflow" : false});
        }
    });
